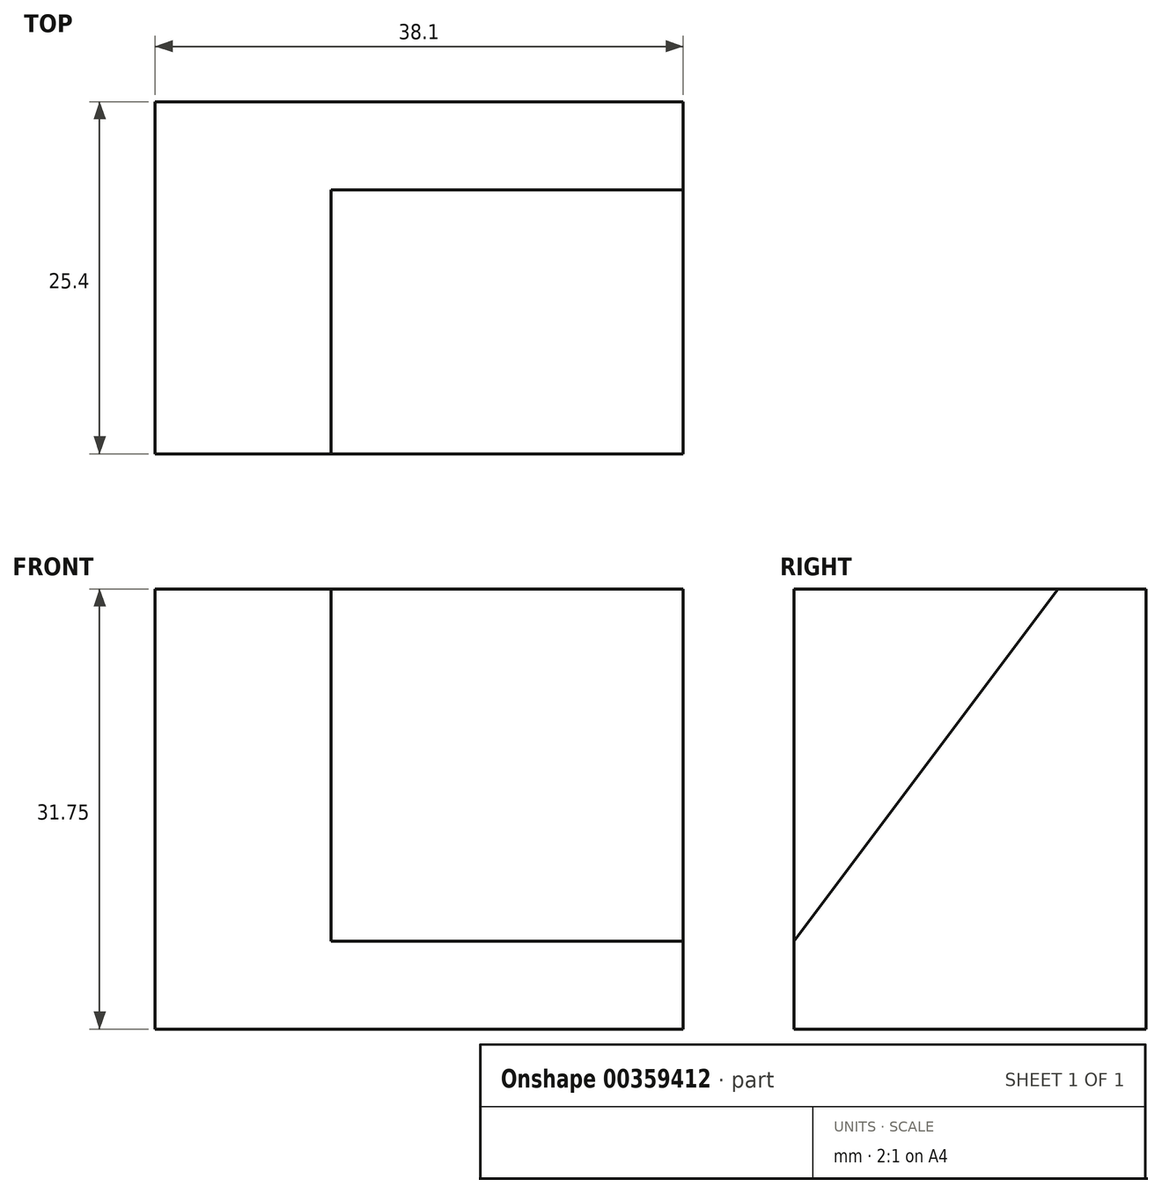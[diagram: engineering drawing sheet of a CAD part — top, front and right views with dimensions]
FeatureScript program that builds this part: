
annotation { "Feature Type Name" : "Feature", "Feature Type Description" : "" }
export const myFeature = defineFeature(function(context is Context, id is Id, definition is map)
    precondition{}
    {
        {
            var Q0;
            Q0=qCreatedBy(makeId("Front.planeOp"),FACE);
            var sketch = newSketch(context, id + "F0", { "sketchPlane" : qUnion([Q0])});
            skLineSegment(sketch, "E0", {"start": v(0, 0) * mm, "end": v(0, 31.75) * mm});
            skLineSegment(sketch, "E1", {"start": v(0, 31.75) * mm, "end": v(38.1, 31.75) * mm});
            skLineSegment(sketch, "E2", {"start": v(38.1, 31.75) * mm, "end": v(38.1, 0) * mm});
            skLineSegment(sketch, "E3", {"start": v(38.1, 0) * mm, "end": v(0, 0) * mm});
            skSolve(sketch);
        }
        {
            var Q0;
            Q0=makeQuery(id+"F0.imprint","IMPRINT",FACE,{"disambiguationData":[TD([[makeQuery(id+"F0.imprint","IMPRINT",EDGE,{"derivedFrom":sQuery(id+"F0.wireOp",EDGE,"E0")}),-1.0]])]});
            extrude(context, id + "F1", {"entities" : qUnion([Q0]), "depth" : 25.4 * mm});
        }
        {
            var Q0;
            Q0=makeQuery(id+"F1.opExtrude","SWEPT_FACE",FACE,{"disambiguationData":[OSD([sQuery(id+"F0.wireOp",EDGE,"E2")])]});
            var sketch = newSketch(context, id + "F2", { "sketchPlane" : qUnion([Q0])});
            skLineSegment(sketch, "E4", {"start": v(-6.35, 31.75) * mm, "end": v(-6.35, 0) * mm});
            skLineSegment(sketch, "E5", {"start": v(-25.4, 6.35) * mm, "end": v(0, 6.35) * mm});
            skLineSegment(sketch, "E6", {"start": v(-25.4, 6.35) * mm, "end": v(-25.4, 0) * mm});
            skLineSegment(sketch, "E7", {"start": v(-6.35, 31.75) * mm, "end": v(0, 31.75) * mm});
            skLineSegment(sketch, "E8", {"start": v(-25.4, 6.35) * mm, "end": v(-6.35, 31.75) * mm});
            skLineSegment(sketch, "E9", {"start": v(-6.35, 31.75) * mm, "end": v(-25.4, 31.75) * mm});
            skLineSegment(sketch, "E10", {"start": v(-25.4, 31.75) * mm, "end": v(-25.4, 6.35) * mm});
            skSolve(sketch);
        }
        {
            var Q0;
            Q0=makeQuery(id+"F2.imprint","IMPRINT",FACE,{"disambiguationData":[TD([[makeQuery(id+"F2.imprint","IMPRINT",EDGE,{"derivedFrom":sQuery(id+"F2.wireOp",EDGE,"E8")}),1.0]])]});
            extrude(context, id + "F3", {"entities" : qUnion([Q0]), "operationType" : NewBodyOperationType.REMOVE, "oppositeDirection" : true, "depth" : 25.4 * mm});
        }
    });
